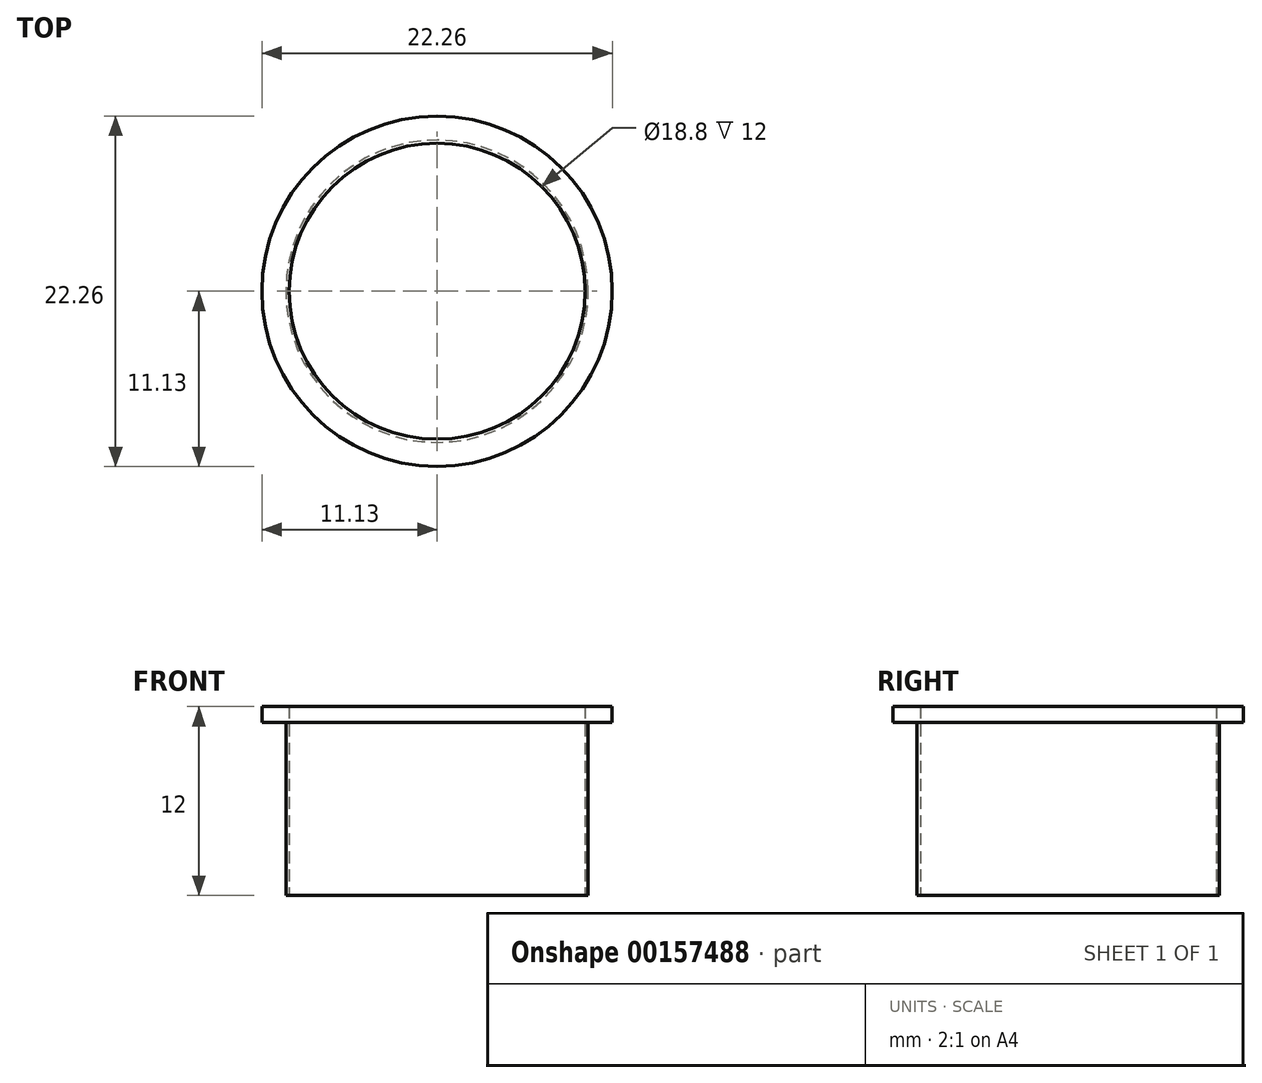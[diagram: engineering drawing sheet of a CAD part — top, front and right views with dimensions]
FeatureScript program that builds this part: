
annotation { "Feature Type Name" : "Feature", "Feature Type Description" : "" }
export const myFeature = defineFeature(function(context is Context, id is Id, definition is map)
    precondition{}
    {
        {
            var Q0;
            Q0=qCreatedBy(makeId("Top.planeOp"),FACE);
            var sketch = newSketch(context, id + "F0", { "sketchPlane" : qUnion([Q0])});
            skCircle(sketch, "E0", {"center": v(0, 0) * mm, "radius": 9.6 * mm});
            skSolve(sketch);
        }
        {
            var Q0;
            Q0 = qSketchRegion(id + "F0", true);
            extrude(context, id + "F1", {"entities" : qUnion([Q0]), "depth" : 11 * mm});
        }
        {
            var Q0;
            Q0=makeQuery(id+"F1.opExtrude","CAP_FACE",FACE,{"disambiguationData":[OSD([sQuery(id+"F0.wireOp",EDGE,"E0")])],"isStart":false});
            var sketch = newSketch(context, id + "F2", { "sketchPlane" : qUnion([Q0])});
            skCircle(sketch, "E1", {"center": v(0, 0) * mm, "radius": 11.12 * mm});
            skSolve(sketch);
        }
        {
            var Q0;
            Q0 = qSketchRegion(id + "F2", true);
            extrude(context, id + "F3", {"entities" : qUnion([Q0]), "operationType" : NewBodyOperationType.ADD, "depth" : 1 * mm});
        }
        {
            var Q0;
            Q0=makeQuery(id+"F1.opExtrude","CAP_FACE",FACE,{"disambiguationData":[OSD([sQuery(id+"F0.wireOp",EDGE,"E0")])],"isStart":true});
            var sketch = newSketch(context, id + "F4", { "sketchPlane" : qUnion([Q0])});
            skCircle(sketch, "E2", {"center": v(0, 0) * mm, "radius": 9.4 * mm});
            skSolve(sketch);
        }
        {
            var Q0;
            Q0 = qSketchRegion(id + "F4", true);
            extrude(context, id + "F5", {"entities" : qUnion([Q0]), "operationType" : NewBodyOperationType.REMOVE, "endBound" : BoundingType.THROUGH_ALL, "oppositeDirection" : true, "depth" : 25 * mm});
        }
    });
